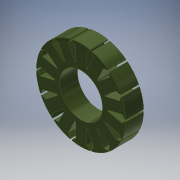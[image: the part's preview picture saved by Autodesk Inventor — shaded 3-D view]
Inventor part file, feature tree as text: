
AUTODESK INVENTOR PART (.ipt)
format: ipt  version: 2019.4 (Build 234330000, 330)  size: 241,152 bytes
history: native  units: mm
features: extrude x3, sketch x3, mirror x1, pattern_circular x1
ambient origin geometry x8: Origin, YZ Plane, XZ Plane, XY Plane, X Axis, Y Axis, Z Axis, Center Point
bodies: Solid1 (feature_tree)
feature tree (8):
  extrude  "Extrusion1"  Depth=30.0mm
  extrude  "Extrusion2"  Depth=10.0mm
  mirror  "Mirror1"
  pattern_circular  "Circular Pattern1"  [2 undecoded]
  extrude  "Extrusion3"  Depth=6.0mm
  sketch  "Sketch1"  dims[d0=50.0mm d1=30.0mm]
  sketch  "Sketch2"  dims[d2=8.0mm d3=4.0mm d4=10.0mm d5=5.0mm]
  sketch  "Sketch3"  dims[d6=2.0mm d7=10.0mm d8=0.0mm d9=6.0mm d10=3.0mm d11=0.5mm d12=10.0mm d13=0.0mm d14=140.0mm d15=360.0deg d17=24.0mm d18=10.0mm d19=0.0mm]
note: 2 required parameter values undecoded (feature->parameter linkage not recoverable at this tier; creation-order binding heuristic only, values carry confidence <= 0.55)
